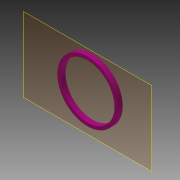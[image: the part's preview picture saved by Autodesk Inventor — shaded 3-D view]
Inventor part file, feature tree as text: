
AUTODESK INVENTOR PART (.ipt)
format: ipt  version: 2014 (Build 180170000, 170)  size: 86,016 bytes
history: native  units: in
note: dims shown in document units (in); Inventor stores cm internally (conversion verified against a paired STEP export)
features: reference x2, plane x1, extrude x1, sketch x1
ambient origin geometry x8: Origin, YZ Plane, XZ Plane, XY Plane, X Axis, Y Axis, Z Axis, Center Point
bodies: Solid1 (feature_tree)
feature tree (5):
  plane  "Work Plane1"
  extrude  "Extrusion1"  Depth=0.15in TaperAngle=0.0deg
  sketch  "Sketch1"  dims[d0=0.1in d1=0.15in d2=0.0in]
  reference  "Reference1"
  reference  "Reference2"
